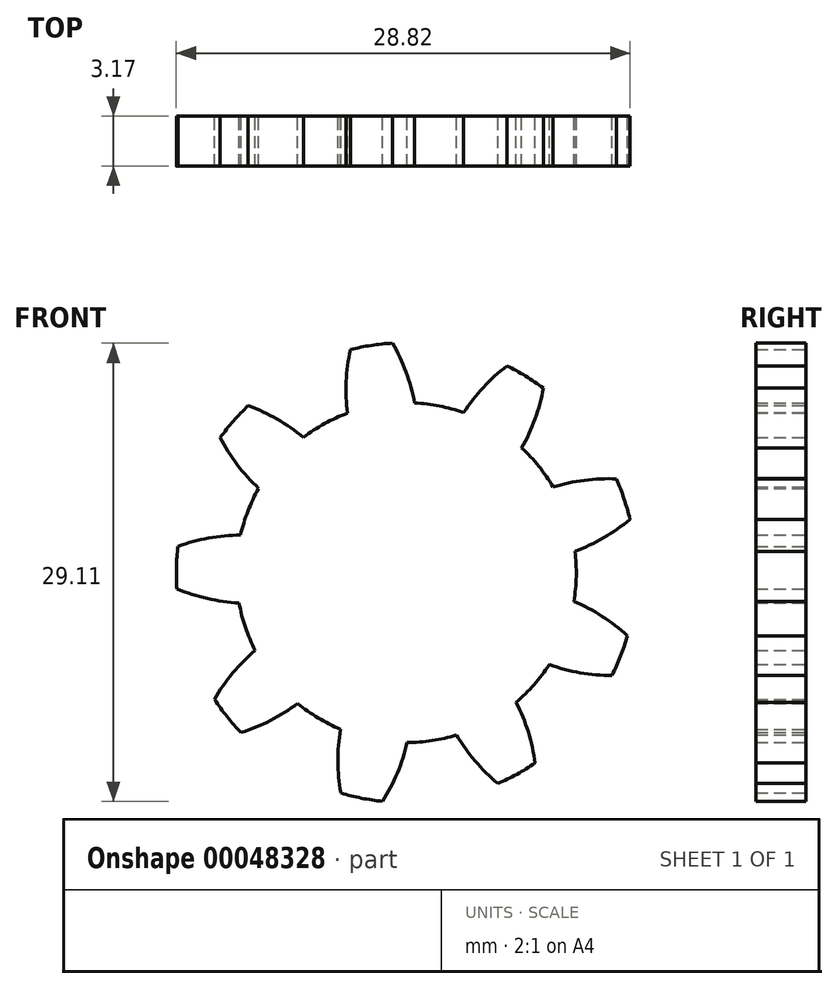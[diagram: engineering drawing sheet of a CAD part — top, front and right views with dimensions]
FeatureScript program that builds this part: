
annotation { "Feature Type Name" : "Feature", "Feature Type Description" : "" }
export const myFeature = defineFeature(function(context is Context, id is Id, definition is map)
    precondition{}
    {
        {
            var Q0;
            Q0=qCreatedBy(makeId("Front.planeOp"),FACE);
            var sketch = newSketch(context, id + "F0", { "sketchPlane" : qUnion([Q0])});
            skCircle(sketch, "E0", {"center": v(0, 0) * mm, "radius": 10.8 * mm});
            skCircle(sketch, "E1", {"center": v(0, 0) * mm, "radius": 12.7 * mm, "construction": true});
            skLineSegment(sketch, "E2", {"start": v(0, 0) * mm, "end": v(0, 26.15) * mm, "construction": true});
            skLineSegment(sketch, "E3", {"start": v(0, 0) * mm, "end": v(-3.96, 25.7) * mm, "construction": true});
            skLineSegment(sketch, "E4", {"start": v(0, 12.7) * mm, "end": v(-26.76, 12.7) * mm, "construction": true});
            skLineSegment(sketch, "E5", {"start": v(0, 12.7) * mm, "end": v(-29.82, 1.85) * mm, "construction": true});
            skCircle(sketch, "E6", {"center": v(0, 12.7) * mm, "radius": 11.93 * mm, "construction": true});
            skArc(sketch, "E7", {"start": v(0.52, 10.78) * mm, "mid": v(-0.01, 12.74) * mm, "end": v(-0.88, 14.58) * mm});
            skArc(sketch, "E8", {"start": v(-0.88, 14.58) * mm, "mid": v(-22.4, 4.5) * mm, "end": v(0.52, 10.78) * mm, "construction": true});
            skArc(sketch, "E9.MirrorCS", {"start": v(-3.74, 10.13) * mm, "mid": v(-3.82, 12.16) * mm, "end": v(-3.55, 14.17) * mm});
            skLineSegment(sketch, "E10", {"start": v(-0.88, 14.58) * mm, "end": v(-0.88, 14.58) * mm});
            skArc(sketch, "E11", {"start": v(-0.88, 14.58) * mm, "mid": v(-2.22, 14.44) * mm, "end": v(-3.55, 14.17) * mm});
            skArc(sketch, "E12", {"start": v(-3.55, 14.17) * mm, "mid": v(2.22, -14.44) * mm, "end": v(-0.88, 14.58) * mm, "construction": true});
            skArc(sketch, "E13.1.0", {"start": v(-10.04, 10.6) * mm, "mid": v(-10.98, 9.63) * mm, "end": v(-11.83, 8.57) * mm});
            skArc(sketch, "E13.1.1", {"start": v(-6.53, 8.6) * mm, "mid": v(-8.2, 9.75) * mm, "end": v(-10.04, 10.6) * mm});
            skArc(sketch, "E13.1.2", {"start": v(-9.37, 5.35) * mm, "mid": v(-10.74, 6.86) * mm, "end": v(-11.83, 8.57) * mm});
            skArc(sketch, "E13.2.0", {"start": v(-14.5, 1.67) * mm, "mid": v(-14.6, 0.32) * mm, "end": v(-14.57, -1.03) * mm});
            skArc(sketch, "E13.2.1", {"start": v(-10.53, 2.39) * mm, "mid": v(-12.55, 2.2) * mm, "end": v(-14.5, 1.67) * mm});
            skArc(sketch, "E13.2.2", {"start": v(-10.62, -1.92) * mm, "mid": v(-12.63, -1.65) * mm, "end": v(-14.57, -1.03) * mm});
            skArc(sketch, "E13.3.0", {"start": v(-12.19, -8.05) * mm, "mid": v(-11.4, -9.14) * mm, "end": v(-10.5, -10.16) * mm});
            skArc(sketch, "E13.3.1", {"start": v(-9.6, -4.94) * mm, "mid": v(-11.03, -6.38) * mm, "end": v(-12.19, -8.05) * mm});
            skArc(sketch, "E13.3.2", {"start": v(-6.9, -8.3) * mm, "mid": v(-8.62, -9.38) * mm, "end": v(-10.5, -10.16) * mm});
            skArc(sketch, "E13.4.0", {"start": v(-4.16, -14) * mm, "mid": v(-2.85, -14.32) * mm, "end": v(-1.51, -14.53) * mm});
            skArc(sketch, "E13.4.1", {"start": v(-4.18, -9.95) * mm, "mid": v(-4.34, -11.98) * mm, "end": v(-4.16, -14) * mm});
            skArc(sketch, "E13.4.2", {"start": v(0.05, -10.8) * mm, "mid": v(-0.57, -12.73) * mm, "end": v(-1.51, -14.53) * mm});
            skArc(sketch, "E13.5.0", {"start": v(5.8, -13.4) * mm, "mid": v(7.02, -12.8) * mm, "end": v(8.18, -12.1) * mm});
            skArc(sketch, "E13.5.1", {"start": v(3.2, -10.31) * mm, "mid": v(4.37, -11.97) * mm, "end": v(5.8, -13.4) * mm});
            skArc(sketch, "E13.5.2", {"start": v(6.98, -8.24) * mm, "mid": v(7.74, -10.12) * mm, "end": v(8.18, -12.1) * mm});
            skArc(sketch, "E13.6.0", {"start": v(13.06, -6.53) * mm, "mid": v(13.61, -5.3) * mm, "end": v(14.04, -4.01) * mm});
            skArc(sketch, "E13.6.1", {"start": v(9.08, -5.84) * mm, "mid": v(11.04, -6.36) * mm, "end": v(13.06, -6.53) * mm});
            skArc(sketch, "E13.6.2", {"start": v(10.64, -1.82) * mm, "mid": v(12.44, -2.77) * mm, "end": v(14.04, -4.01) * mm});
            skArc(sketch, "E13.7.0", {"start": v(14.2, 3.4) * mm, "mid": v(13.83, 4.7) * mm, "end": v(13.34, 5.96) * mm});
            skArc(sketch, "E13.7.1", {"start": v(10.7, 1.36) * mm, "mid": v(12.54, 2.23) * mm, "end": v(14.2, 3.4) * mm});
            skArc(sketch, "E13.7.2", {"start": v(9.32, 5.44) * mm, "mid": v(11.3, 5.87) * mm, "end": v(13.34, 5.96) * mm});
            skArc(sketch, "E13.8.0", {"start": v(8.7, 11.73) * mm, "mid": v(7.58, 12.49) * mm, "end": v(6.39, 13.13) * mm});
            skArc(sketch, "E13.8.1", {"start": v(7.33, 7.92) * mm, "mid": v(8.18, 9.77) * mm, "end": v(8.7, 11.73) * mm});
            skArc(sketch, "E13.8.2", {"start": v(3.64, 10.16) * mm, "mid": v(4.89, 11.76) * mm, "end": v(6.39, 13.13) * mm});
            skSolve(sketch);
        }
        {
            var Q0;
            {var subQ0=sQuery(id+"F0.wireOp",EDGE,"E0");var subQ3=makeQuery(id+"F0.imprint","INTERSECT",VERTEX,{"derivedFrom":[subQ0,sQuery(id+"F0.wireOp",EDGE,"E13.7.1")]});Q0=makeQuery(id+"F0.imprint","IMPRINT",FACE,{"disambiguationData":[TD([[makeQuery(id+"F0.imprint","IMPRINT",EDGE,{"disambiguationData":[TD([[subQ3,-1.0]])],"derivedFrom":subQ0}),1.0]])]});}
            var Q1;
            Q1=makeQuery(id+"F0.imprint","IMPRINT",FACE,{"disambiguationData":[TD([[makeQuery(id+"F0.imprint","IMPRINT",EDGE,{"derivedFrom":sQuery(id+"F0.wireOp",EDGE,"E13.2.0")}),1.0]])]});
            var Q2;
            Q2=makeQuery(id+"F0.imprint","IMPRINT",FACE,{"disambiguationData":[TD([[makeQuery(id+"F0.imprint","IMPRINT",EDGE,{"derivedFrom":sQuery(id+"F0.wireOp",EDGE,"E13.1.0")}),1.0]])]});
            var Q3;
            {var subQ0=sQuery(id+"F0.wireOp",EDGE,"E7");Q3=makeQuery(id+"F0.imprint","IMPRINT",FACE,{"disambiguationData":[TD([[makeQuery(id+"F0.imprint","IMPRINT",EDGE,{"derivedFrom":subQ0}),1.0]])]});}
            var Q4;
            Q4=makeQuery(id+"F0.imprint","IMPRINT",FACE,{"disambiguationData":[TD([[makeQuery(id+"F0.imprint","IMPRINT",EDGE,{"derivedFrom":sQuery(id+"F0.wireOp",EDGE,"E13.8.0")}),1.0]])]});
            var Q5;
            Q5=makeQuery(id+"F0.imprint","IMPRINT",FACE,{"disambiguationData":[TD([[makeQuery(id+"F0.imprint","IMPRINT",EDGE,{"derivedFrom":sQuery(id+"F0.wireOp",EDGE,"E13.7.0")}),1.0]])]});
            var Q6;
            Q6=makeQuery(id+"F0.imprint","IMPRINT",FACE,{"disambiguationData":[TD([[makeQuery(id+"F0.imprint","IMPRINT",EDGE,{"derivedFrom":sQuery(id+"F0.wireOp",EDGE,"E13.6.0")}),1.0]])]});
            var Q7;
            Q7=makeQuery(id+"F0.imprint","IMPRINT",FACE,{"disambiguationData":[TD([[makeQuery(id+"F0.imprint","IMPRINT",EDGE,{"derivedFrom":sQuery(id+"F0.wireOp",EDGE,"E13.5.0")}),1.0]])]});
            var Q8;
            Q8=makeQuery(id+"F0.imprint","IMPRINT",FACE,{"disambiguationData":[TD([[makeQuery(id+"F0.imprint","IMPRINT",EDGE,{"derivedFrom":sQuery(id+"F0.wireOp",EDGE,"E13.4.0")}),1.0]])]});
            var Q9;
            Q9=makeQuery(id+"F0.imprint","IMPRINT",FACE,{"disambiguationData":[TD([[makeQuery(id+"F0.imprint","IMPRINT",EDGE,{"derivedFrom":sQuery(id+"F0.wireOp",EDGE,"E13.3.0")}),1.0]])]});
            extrude(context, id + "F1", {"entities" : qUnion([Q0, Q1, Q2, Q3, Q4, Q5, Q6, Q7, Q8, Q9]), "depth" : 3.17 * mm});
        }
    });
